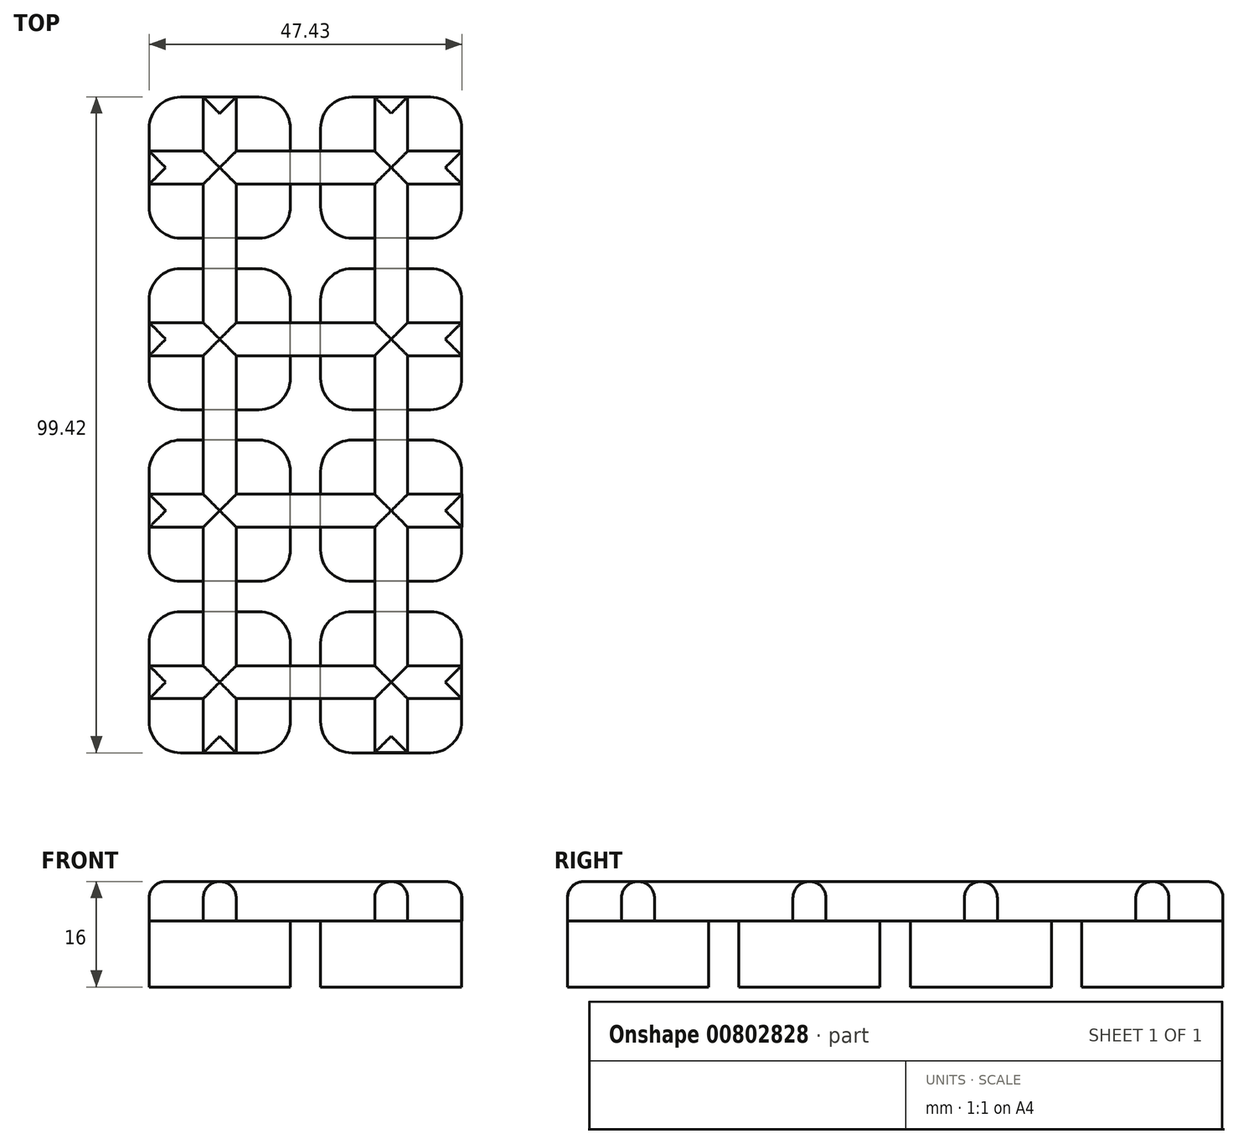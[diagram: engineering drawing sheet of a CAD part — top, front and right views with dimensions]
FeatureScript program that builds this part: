
annotation { "Feature Type Name" : "Feature", "Feature Type Description" : "" }
export const myFeature = defineFeature(function(context is Context, id is Id, definition is map)
    precondition{}
    {
        {
            var Q0;
            Q0=qCreatedBy(makeId("Top.planeOp"),FACE);
            var sketch = newSketch(context, id + "F0", { "sketchPlane" : qUnion([Q0])});
            skLineSegment(sketch, "E0.bottom", {"start": v(10.7, -10.7) * mm, "end": v(-10.7, -10.7) * mm});
            skLineSegment(sketch, "E0.top", {"start": v(10.7, 10.7) * mm, "end": v(-10.7, 10.7) * mm});
            skLineSegment(sketch, "E0.left", {"start": v(10.7, -10.7) * mm, "end": v(10.7, 10.7) * mm});
            skLineSegment(sketch, "E0.right", {"start": v(-10.7, -10.7) * mm, "end": v(-10.7, 10.7) * mm});
            skPoint(sketch, "E0.middle", {"position": v(0, 0) * mm});
            skLineSegment(sketch, "E1.bottom", {"start": v(36.7, -10.7) * mm, "end": v(15.3, -10.7) * mm});
            skLineSegment(sketch, "E1.top", {"start": v(36.7, 10.7) * mm, "end": v(15.3, 10.7) * mm});
            skLineSegment(sketch, "E1.left", {"start": v(36.7, -10.7) * mm, "end": v(36.7, 10.7) * mm});
            skLineSegment(sketch, "E1.right", {"start": v(15.3, -10.7) * mm, "end": v(15.3, 10.7) * mm});
            skPoint(sketch, "E1.middle", {"position": v(26, 0) * mm});
            skLineSegment(sketch, "E2.bottom", {"start": v(10.7, -36.7) * mm, "end": v(-10.7, -36.7) * mm});
            skLineSegment(sketch, "E2.top", {"start": v(10.7, -15.3) * mm, "end": v(-10.7, -15.3) * mm});
            skLineSegment(sketch, "E2.left", {"start": v(10.7, -36.7) * mm, "end": v(10.7, -15.3) * mm});
            skLineSegment(sketch, "E2.right", {"start": v(-10.7, -36.7) * mm, "end": v(-10.7, -15.3) * mm});
            skPoint(sketch, "E2.middle", {"position": v(0, -26) * mm});
            skLineSegment(sketch, "E3.bottom", {"start": v(36.7, -36.7) * mm, "end": v(15.3, -36.7) * mm});
            skLineSegment(sketch, "E3.top", {"start": v(36.7, -15.3) * mm, "end": v(15.3, -15.3) * mm});
            skLineSegment(sketch, "E3.left", {"start": v(36.7, -36.7) * mm, "end": v(36.7, -15.3) * mm});
            skLineSegment(sketch, "E3.right", {"start": v(15.3, -36.7) * mm, "end": v(15.3, -15.3) * mm});
            skPoint(sketch, "E3.middle", {"position": v(26, -26) * mm});
            skLineSegment(sketch, "E4.bottom", {"start": v(10.7, -62.7) * mm, "end": v(-10.7, -62.7) * mm});
            skLineSegment(sketch, "E4.top", {"start": v(10.7, -41.3) * mm, "end": v(-10.7, -41.3) * mm});
            skLineSegment(sketch, "E4.left", {"start": v(10.7, -62.7) * mm, "end": v(10.7, -41.3) * mm});
            skLineSegment(sketch, "E4.right", {"start": v(-10.7, -62.7) * mm, "end": v(-10.7, -41.3) * mm});
            skPoint(sketch, "E4.middle", {"position": v(0, -52) * mm});
            skLineSegment(sketch, "E5.bottom", {"start": v(36.7, -62.7) * mm, "end": v(15.3, -62.7) * mm});
            skLineSegment(sketch, "E5.top", {"start": v(36.7, -41.3) * mm, "end": v(15.3, -41.3) * mm});
            skLineSegment(sketch, "E5.left", {"start": v(36.7, -62.7) * mm, "end": v(36.7, -41.3) * mm});
            skLineSegment(sketch, "E5.right", {"start": v(15.3, -62.7) * mm, "end": v(15.3, -41.3) * mm});
            skPoint(sketch, "E5.middle", {"position": v(26, -52) * mm});
            skLineSegment(sketch, "E6.bottom", {"start": v(10.7, -88.7) * mm, "end": v(-10.7, -88.7) * mm});
            skLineSegment(sketch, "E6.top", {"start": v(10.7, -67.3) * mm, "end": v(-10.7, -67.3) * mm});
            skLineSegment(sketch, "E6.left", {"start": v(10.7, -88.7) * mm, "end": v(10.7, -67.3) * mm});
            skLineSegment(sketch, "E6.right", {"start": v(-10.7, -88.7) * mm, "end": v(-10.7, -67.3) * mm});
            skPoint(sketch, "E6.middle", {"position": v(0, -78) * mm});
            skLineSegment(sketch, "E7.bottom", {"start": v(36.7, -88.7) * mm, "end": v(15.3, -88.7) * mm});
            skLineSegment(sketch, "E7.top", {"start": v(36.7, -67.3) * mm, "end": v(15.3, -67.3) * mm});
            skLineSegment(sketch, "E7.left", {"start": v(36.7, -88.7) * mm, "end": v(36.7, -67.3) * mm});
            skLineSegment(sketch, "E7.right", {"start": v(15.3, -88.7) * mm, "end": v(15.3, -67.3) * mm});
            skPoint(sketch, "E7.middle", {"position": v(26, -78) * mm});
            skSolve(sketch);
        }
        {
            var Q0;
            Q0 = qSketchRegion(id + "F0", true);
            extrude(context, id + "F1", {"entities" : qUnion([Q0]), "depth" : 10 * mm, "offsetDistance" : 25 * mm});
        }
        {
            var Q0;
            Q0=makeQuery(id+"F1.opExtrude","CAP_FACE",FACE,{"disambiguationData":[OSD([sQuery(id+"F0.wireOp",EDGE,"E0.bottom"),sQuery(id+"F0.wireOp",EDGE,"E0.top"),sQuery(id+"F0.wireOp",EDGE,"E0.left"),sQuery(id+"F0.wireOp",EDGE,"E0.right")])],"isStart":false});
            var sketch = newSketch(context, id + "F2", { "sketchPlane" : qUnion([Q0])});
            skLineSegment(sketch, "E8.bottom", {"start": v(-10.7, 2.5) * mm, "end": v(-2.5, 2.5) * mm});
            skLineSegment(sketch, "E8.top", {"start": v(-10.7, -2.5) * mm, "end": v(-2.5, -2.5) * mm});
            skLineSegment(sketch, "E8.left", {"start": v(-10.7, 2.5) * mm, "end": v(-10.7, -2.5) * mm});
            skLineSegment(sketch, "E8.right", {"start": v(36.7, 2.5) * mm, "end": v(36.7, -2.5) * mm});
            skLineSegment(sketch, "E9.bottom", {"start": v(-2.5, 10.7) * mm, "end": v(2.5, 10.7) * mm});
            skLineSegment(sketch, "E9.top", {"start": v(-2.5, -88.7) * mm, "end": v(2.5, -88.7) * mm});
            skLineSegment(sketch, "E9.left", {"start": v(-2.5, 10.7) * mm, "end": v(-2.5, 2.5) * mm});
            skLineSegment(sketch, "E9.right", {"start": v(2.5, 10.7) * mm, "end": v(2.5, 2.5) * mm});
            skLineSegment(sketch, "E10.bottom", {"start": v(23.5, 10.72) * mm, "end": v(28.5, 10.72) * mm});
            skLineSegment(sketch, "E10.top", {"start": v(23.5, -88.68) * mm, "end": v(28.5, -88.68) * mm});
            skLineSegment(sketch, "E10.left", {"start": v(23.5, 10.72) * mm, "end": v(23.5, 2.5) * mm});
            skLineSegment(sketch, "E10.right", {"start": v(28.5, 10.72) * mm, "end": v(28.5, 2.5) * mm});
            skLineSegment(sketch, "E11.bottom", {"start": v(-10.7, -23.5) * mm, "end": v(-2.5, -23.5) * mm});
            skLineSegment(sketch, "E11.top", {"start": v(-10.7, -28.5) * mm, "end": v(-2.5, -28.5) * mm});
            skLineSegment(sketch, "E11.left", {"start": v(-10.7, -23.5) * mm, "end": v(-10.7, -28.5) * mm});
            skLineSegment(sketch, "E11.right", {"start": v(36.7, -23.5) * mm, "end": v(36.7, -28.5) * mm});
            skLineSegment(sketch, "E12.bottom", {"start": v(-10.67, -49.5) * mm, "end": v(-2.5, -49.5) * mm});
            skLineSegment(sketch, "E12.top", {"start": v(-10.67, -54.5) * mm, "end": v(-2.5, -54.5) * mm});
            skLineSegment(sketch, "E12.left", {"start": v(-10.67, -49.5) * mm, "end": v(-10.67, -54.5) * mm});
            skLineSegment(sketch, "E12.right", {"start": v(36.73, -49.5) * mm, "end": v(36.73, -54.5) * mm});
            skLineSegment(sketch, "E13.bottom", {"start": v(-10.7, -75.5) * mm, "end": v(-2.5, -75.5) * mm});
            skLineSegment(sketch, "E13.top", {"start": v(-10.7, -80.5) * mm, "end": v(-2.5, -80.5) * mm});
            skLineSegment(sketch, "E13.left", {"start": v(-10.7, -75.5) * mm, "end": v(-10.7, -80.5) * mm});
            skLineSegment(sketch, "E13.right", {"start": v(36.7, -75.5) * mm, "end": v(36.7, -80.5) * mm});
            skLineSegment(sketch, "E14.trimOffspring", {"start": v(-2.5, -28.5) * mm, "end": v(-2.5, -49.5) * mm});
            skLineSegment(sketch, "E15.trimOffspring", {"start": v(2.5, -23.5) * mm, "end": v(23.5, -23.5) * mm});
            skLineSegment(sketch, "E16.trimOffspring", {"start": v(2.5, -28.5) * mm, "end": v(2.5, -49.5) * mm});
            skLineSegment(sketch, "E17.trimOffspring", {"start": v(2.5, -28.5) * mm, "end": v(23.5, -28.5) * mm});
            skLineSegment(sketch, "E18.trimOffspring", {"start": v(28.5, -23.5) * mm, "end": v(36.7, -23.5) * mm});
            skLineSegment(sketch, "E19.trimOffspring", {"start": v(23.5, -28.5) * mm, "end": v(23.5, -49.5) * mm});
            skLineSegment(sketch, "E20.trimOffspring", {"start": v(28.5, -28.5) * mm, "end": v(36.7, -28.5) * mm});
            skLineSegment(sketch, "E21.trimOffspring", {"start": v(28.5, -28.5) * mm, "end": v(28.5, -49.5) * mm});
            skLineSegment(sketch, "E22.trimOffspring", {"start": v(28.5, -49.5) * mm, "end": v(36.73, -49.5) * mm});
            skLineSegment(sketch, "E23.trimOffspring", {"start": v(23.5, -54.5) * mm, "end": v(23.5, -75.5) * mm});
            skLineSegment(sketch, "E24.trimOffspring", {"start": v(28.5, -54.5) * mm, "end": v(28.5, -75.5) * mm});
            skLineSegment(sketch, "E25.trimOffspring", {"start": v(28.5, -54.5) * mm, "end": v(36.73, -54.5) * mm});
            skLineSegment(sketch, "E26.trimOffspring", {"start": v(-2.5, -54.5) * mm, "end": v(-2.5, -75.5) * mm});
            skLineSegment(sketch, "E27.trimOffspring", {"start": v(2.5, -49.5) * mm, "end": v(23.5, -49.5) * mm});
            skLineSegment(sketch, "E28.trimOffspring", {"start": v(2.5, -54.5) * mm, "end": v(2.5, -75.5) * mm});
            skLineSegment(sketch, "E29.trimOffspring", {"start": v(2.5, -54.5) * mm, "end": v(23.5, -54.5) * mm});
            skLineSegment(sketch, "E30.trimOffspring", {"start": v(2.5, -75.5) * mm, "end": v(23.5, -75.5) * mm});
            skLineSegment(sketch, "E31.trimOffspring", {"start": v(-2.5, -80.5) * mm, "end": v(-2.5, -88.7) * mm});
            skLineSegment(sketch, "E32.trimOffspring", {"start": v(2.5, -80.5) * mm, "end": v(23.5, -80.5) * mm});
            skLineSegment(sketch, "E33.trimOffspring", {"start": v(2.5, -80.5) * mm, "end": v(2.5, -88.7) * mm});
            skLineSegment(sketch, "E34.trimOffspring", {"start": v(23.5, -80.5) * mm, "end": v(23.5, -88.68) * mm});
            skLineSegment(sketch, "E35.trimOffspring", {"start": v(28.5, -75.5) * mm, "end": v(36.7, -75.5) * mm});
            skLineSegment(sketch, "E36.trimOffspring", {"start": v(28.5, -80.5) * mm, "end": v(28.5, -88.68) * mm});
            skLineSegment(sketch, "E37.trimOffspring", {"start": v(28.5, -80.5) * mm, "end": v(36.7, -80.5) * mm});
            skLineSegment(sketch, "E38.trimOffspring", {"start": v(2.5, 2.5) * mm, "end": v(23.5, 2.5) * mm});
            skLineSegment(sketch, "E39.trimOffspring", {"start": v(-2.5, -2.5) * mm, "end": v(-2.5, -23.5) * mm});
            skLineSegment(sketch, "E40.trimOffspring", {"start": v(2.5, -2.5) * mm, "end": v(23.5, -2.5) * mm});
            skLineSegment(sketch, "E41.trimOffspring", {"start": v(2.5, -2.5) * mm, "end": v(2.5, -23.5) * mm});
            skLineSegment(sketch, "E42.trimOffspring", {"start": v(23.5, -2.5) * mm, "end": v(23.5, -23.5) * mm});
            skLineSegment(sketch, "E43.trimOffspring", {"start": v(28.5, 2.5) * mm, "end": v(36.7, 2.5) * mm});
            skLineSegment(sketch, "E44.trimOffspring", {"start": v(28.5, -2.5) * mm, "end": v(28.5, -23.5) * mm});
            skLineSegment(sketch, "E45.trimOffspring", {"start": v(28.5, -2.5) * mm, "end": v(36.7, -2.5) * mm});
            skSolve(sketch);
        }
        {
            var Q0;
            Q0 = qSketchRegion(id + "F2", true);
            extrude(context, id + "F3", {"entities" : qUnion([Q0]), "depth" : 6 * mm, "offsetDistance" : 25 * mm});
        }
        {
            var Q0;
            Q0=makeQuery(id+"F1.opExtrude","SWEPT_EDGE",EDGE,{"disambiguationData":[OSD([sQuery(id+"F0.wireOp",EDGE,"E7.bottom"),sQuery(id+"F0.wireOp",EDGE,"E7.left")])]});
            var Q1;
            Q1=makeQuery(id+"F1.opExtrude","SWEPT_EDGE",EDGE,{"disambiguationData":[OSD([sQuery(id+"F0.wireOp",EDGE,"E7.bottom"),sQuery(id+"F0.wireOp",EDGE,"E7.right")])]});
            var Q2;
            Q2=makeQuery(id+"F1.opExtrude","SWEPT_EDGE",EDGE,{"disambiguationData":[OSD([sQuery(id+"F0.wireOp",EDGE,"E6.bottom"),sQuery(id+"F0.wireOp",EDGE,"E6.left")])]});
            var Q3;
            Q3=makeQuery(id+"F1.opExtrude","SWEPT_EDGE",EDGE,{"disambiguationData":[OSD([sQuery(id+"F0.wireOp",EDGE,"E6.bottom"),sQuery(id+"F0.wireOp",EDGE,"E6.right")])]});
            var Q4;
            Q4=makeQuery(id+"F1.opExtrude","SWEPT_EDGE",EDGE,{"disambiguationData":[OSD([sQuery(id+"F0.wireOp",EDGE,"E7.top"),sQuery(id+"F0.wireOp",EDGE,"E7.left")])]});
            var Q5;
            Q5=makeQuery(id+"F1.opExtrude","SWEPT_EDGE",EDGE,{"disambiguationData":[OSD([sQuery(id+"F0.wireOp",EDGE,"E5.bottom"),sQuery(id+"F0.wireOp",EDGE,"E5.left")])]});
            var Q6;
            Q6=makeQuery(id+"F1.opExtrude","SWEPT_EDGE",EDGE,{"disambiguationData":[OSD([sQuery(id+"F0.wireOp",EDGE,"E5.top"),sQuery(id+"F0.wireOp",EDGE,"E5.left")])]});
            var Q7;
            Q7=makeQuery(id+"F1.opExtrude","SWEPT_EDGE",EDGE,{"disambiguationData":[OSD([sQuery(id+"F0.wireOp",EDGE,"E3.bottom"),sQuery(id+"F0.wireOp",EDGE,"E3.left")])]});
            var Q8;
            Q8=makeQuery(id+"F1.opExtrude","SWEPT_EDGE",EDGE,{"disambiguationData":[OSD([sQuery(id+"F0.wireOp",EDGE,"E3.top"),sQuery(id+"F0.wireOp",EDGE,"E3.left")])]});
            var Q9;
            Q9=makeQuery(id+"F1.opExtrude","SWEPT_EDGE",EDGE,{"disambiguationData":[OSD([sQuery(id+"F0.wireOp",EDGE,"E1.bottom"),sQuery(id+"F0.wireOp",EDGE,"E1.left")])]});
            var Q10;
            Q10=makeQuery(id+"F1.opExtrude","SWEPT_EDGE",EDGE,{"disambiguationData":[OSD([sQuery(id+"F0.wireOp",EDGE,"E1.top"),sQuery(id+"F0.wireOp",EDGE,"E1.left")])]});
            var Q11;
            Q11=makeQuery(id+"F1.opExtrude","SWEPT_EDGE",EDGE,{"disambiguationData":[OSD([sQuery(id+"F0.wireOp",EDGE,"E4.bottom"),sQuery(id+"F0.wireOp",EDGE,"E4.left")])]});
            var Q12;
            Q12=makeQuery(id+"F1.opExtrude","SWEPT_EDGE",EDGE,{"disambiguationData":[OSD([sQuery(id+"F0.wireOp",EDGE,"E5.bottom"),sQuery(id+"F0.wireOp",EDGE,"E5.right")])]});
            var Q13;
            Q13=makeQuery(id+"F1.opExtrude","SWEPT_EDGE",EDGE,{"disambiguationData":[OSD([sQuery(id+"F0.wireOp",EDGE,"E2.bottom"),sQuery(id+"F0.wireOp",EDGE,"E2.left")])]});
            var Q14;
            Q14=makeQuery(id+"F1.opExtrude","SWEPT_EDGE",EDGE,{"disambiguationData":[OSD([sQuery(id+"F0.wireOp",EDGE,"E3.bottom"),sQuery(id+"F0.wireOp",EDGE,"E3.right")])]});
            var Q15;
            Q15=makeQuery(id+"F1.opExtrude","SWEPT_EDGE",EDGE,{"disambiguationData":[OSD([sQuery(id+"F0.wireOp",EDGE,"E0.bottom"),sQuery(id+"F0.wireOp",EDGE,"E0.left")])]});
            var Q16;
            Q16=makeQuery(id+"F1.opExtrude","SWEPT_EDGE",EDGE,{"disambiguationData":[OSD([sQuery(id+"F0.wireOp",EDGE,"E1.bottom"),sQuery(id+"F0.wireOp",EDGE,"E1.right")])]});
            var Q17;
            Q17=makeQuery(id+"F1.opExtrude","SWEPT_EDGE",EDGE,{"disambiguationData":[OSD([sQuery(id+"F0.wireOp",EDGE,"E2.top"),sQuery(id+"F0.wireOp",EDGE,"E2.left")])]});
            var Q18;
            Q18=makeQuery(id+"F1.opExtrude","SWEPT_EDGE",EDGE,{"disambiguationData":[OSD([sQuery(id+"F0.wireOp",EDGE,"E0.top"),sQuery(id+"F0.wireOp",EDGE,"E0.left")])]});
            var Q19;
            Q19=makeQuery(id+"F1.opExtrude","SWEPT_EDGE",EDGE,{"disambiguationData":[OSD([sQuery(id+"F0.wireOp",EDGE,"E1.top"),sQuery(id+"F0.wireOp",EDGE,"E1.right")])]});
            var Q20;
            Q20=makeQuery(id+"F1.opExtrude","SWEPT_EDGE",EDGE,{"disambiguationData":[OSD([sQuery(id+"F0.wireOp",EDGE,"E3.top"),sQuery(id+"F0.wireOp",EDGE,"E3.right")])]});
            var Q21;
            Q21=makeQuery(id+"F1.opExtrude","SWEPT_EDGE",EDGE,{"disambiguationData":[OSD([sQuery(id+"F0.wireOp",EDGE,"E5.top"),sQuery(id+"F0.wireOp",EDGE,"E5.right")])]});
            var Q22;
            Q22=makeQuery(id+"F1.opExtrude","SWEPT_EDGE",EDGE,{"disambiguationData":[OSD([sQuery(id+"F0.wireOp",EDGE,"E7.top"),sQuery(id+"F0.wireOp",EDGE,"E7.right")])]});
            var Q23;
            Q23=makeQuery(id+"F1.opExtrude","SWEPT_EDGE",EDGE,{"disambiguationData":[OSD([sQuery(id+"F0.wireOp",EDGE,"E4.top"),sQuery(id+"F0.wireOp",EDGE,"E4.right")])]});
            var Q24;
            Q24=makeQuery(id+"F1.opExtrude","SWEPT_EDGE",EDGE,{"disambiguationData":[OSD([sQuery(id+"F0.wireOp",EDGE,"E0.top"),sQuery(id+"F0.wireOp",EDGE,"E0.right")])]});
            var Q25;
            Q25=makeQuery(id+"F1.opExtrude","SWEPT_EDGE",EDGE,{"disambiguationData":[OSD([sQuery(id+"F0.wireOp",EDGE,"E0.bottom"),sQuery(id+"F0.wireOp",EDGE,"E0.right")])]});
            var Q26;
            Q26=makeQuery(id+"F1.opExtrude","SWEPT_EDGE",EDGE,{"disambiguationData":[OSD([sQuery(id+"F0.wireOp",EDGE,"E2.top"),sQuery(id+"F0.wireOp",EDGE,"E2.right")])]});
            var Q27;
            Q27=makeQuery(id+"F1.opExtrude","SWEPT_EDGE",EDGE,{"disambiguationData":[OSD([sQuery(id+"F0.wireOp",EDGE,"E2.bottom"),sQuery(id+"F0.wireOp",EDGE,"E2.right")])]});
            var Q28;
            Q28=makeQuery(id+"F1.opExtrude","SWEPT_EDGE",EDGE,{"disambiguationData":[OSD([sQuery(id+"F0.wireOp",EDGE,"E4.bottom"),sQuery(id+"F0.wireOp",EDGE,"E4.right")])]});
            var Q29;
            Q29=makeQuery(id+"F1.opExtrude","SWEPT_EDGE",EDGE,{"disambiguationData":[OSD([sQuery(id+"F0.wireOp",EDGE,"E4.top"),sQuery(id+"F0.wireOp",EDGE,"E4.left")])]});
            var Q30;
            Q30=makeQuery(id+"F1.opExtrude","SWEPT_EDGE",EDGE,{"disambiguationData":[OSD([sQuery(id+"F0.wireOp",EDGE,"E6.top"),sQuery(id+"F0.wireOp",EDGE,"E6.right")])]});
            var Q31;
            Q31=makeQuery(id+"F1.opExtrude","SWEPT_EDGE",EDGE,{"disambiguationData":[OSD([sQuery(id+"F0.wireOp",EDGE,"E6.top"),sQuery(id+"F0.wireOp",EDGE,"E6.left")])]});
            fillet(context, id + "F4", {"entities" : qUnion([Q0, Q1, Q2, Q3, Q4, Q5, Q6, Q7, Q8, Q9, Q10, Q11, Q12, Q13, Q14, Q15, Q16, Q17, Q18, Q19, Q20, Q21, Q22, Q23, Q24, Q25, Q26, Q27, Q28, Q29, Q30, Q31]), "radius" : 4.75 * mm, "tangentPropagation" : true, "allowEdgeOverflow" : false});
        }
        {
            var Q0;
            Q0=makeQuery(id+"F3.opExtrude","CAP_EDGE",EDGE,{"disambiguationData":[OSD([sQuery(id+"F2.wireOp",EDGE,"E38.trimOffspring")])],"isStart":false});
            var Q1;
            Q1=makeQuery(id+"F3.opExtrude","CAP_EDGE",EDGE,{"disambiguationData":[OSD([sQuery(id+"F2.wireOp",EDGE,"E10.bottom")])],"isStart":false});
            var Q2;
            Q2=makeQuery(id+"F3.opExtrude","CAP_EDGE",EDGE,{"disambiguationData":[OSD([sQuery(id+"F2.wireOp",EDGE,"E10.left")])],"isStart":false});
            var Q3;
            Q3=makeQuery(id+"F3.opExtrude","CAP_EDGE",EDGE,{"disambiguationData":[OSD([sQuery(id+"F2.wireOp",EDGE,"E9.bottom")])],"isStart":false});
            var Q4;
            Q4=makeQuery(id+"F3.opExtrude","CAP_EDGE",EDGE,{"disambiguationData":[OSD([sQuery(id+"F2.wireOp",EDGE,"E11.bottom")])],"isStart":false});
            var Q5;
            Q5=makeQuery(id+"F3.opExtrude","CAP_EDGE",EDGE,{"disambiguationData":[OSD([sQuery(id+"F2.wireOp",EDGE,"E9.left")])],"isStart":false});
            var Q6;
            Q6=makeQuery(id+"F3.opExtrude","CAP_EDGE",EDGE,{"disambiguationData":[OSD([sQuery(id+"F2.wireOp",EDGE,"E9.right")])],"isStart":false});
            var Q7;
            Q7=makeQuery(id+"F3.opExtrude","CAP_EDGE",EDGE,{"disambiguationData":[OSD([sQuery(id+"F2.wireOp",EDGE,"E8.bottom")])],"isStart":false});
            var Q8;
            Q8=makeQuery(id+"F3.opExtrude","CAP_EDGE",EDGE,{"disambiguationData":[OSD([sQuery(id+"F2.wireOp",EDGE,"E10.right")])],"isStart":false});
            var Q9;
            Q9=makeQuery(id+"F3.opExtrude","CAP_EDGE",EDGE,{"disambiguationData":[OSD([sQuery(id+"F2.wireOp",EDGE,"E43.trimOffspring")])],"isStart":false});
            var Q10;
            Q10=makeQuery(id+"F3.opExtrude","CAP_EDGE",EDGE,{"disambiguationData":[OSD([sQuery(id+"F2.wireOp",EDGE,"E8.right")])],"isStart":false});
            var Q11;
            Q11=makeQuery(id+"F3.opExtrude","CAP_EDGE",EDGE,{"disambiguationData":[OSD([sQuery(id+"F2.wireOp",EDGE,"E8.left")])],"isStart":false});
            var Q12;
            Q12=makeQuery(id+"F3.opExtrude","CAP_EDGE",EDGE,{"disambiguationData":[OSD([sQuery(id+"F2.wireOp",EDGE,"E8.top")])],"isStart":false});
            var Q13;
            Q13=makeQuery(id+"F3.opExtrude","CAP_EDGE",EDGE,{"disambiguationData":[OSD([sQuery(id+"F2.wireOp",EDGE,"E39.trimOffspring")])],"isStart":false});
            var Q14;
            Q14=makeQuery(id+"F3.opExtrude","CAP_EDGE",EDGE,{"disambiguationData":[OSD([sQuery(id+"F2.wireOp",EDGE,"E11.left")])],"isStart":false});
            var Q15;
            Q15=makeQuery(id+"F3.opExtrude","CAP_EDGE",EDGE,{"disambiguationData":[OSD([sQuery(id+"F2.wireOp",EDGE,"E11.top")])],"isStart":false});
            var Q16;
            Q16=makeQuery(id+"F3.opExtrude","CAP_EDGE",EDGE,{"disambiguationData":[OSD([sQuery(id+"F2.wireOp",EDGE,"E12.left")])],"isStart":false});
            var Q17;
            Q17=makeQuery(id+"F3.opExtrude","CAP_EDGE",EDGE,{"disambiguationData":[OSD([sQuery(id+"F2.wireOp",EDGE,"E12.bottom")])],"isStart":false});
            var Q18;
            Q18=makeQuery(id+"F3.opExtrude","CAP_EDGE",EDGE,{"disambiguationData":[OSD([sQuery(id+"F2.wireOp",EDGE,"E14.trimOffspring")])],"isStart":false});
            var Q19;
            Q19=makeQuery(id+"F3.opExtrude","CAP_EDGE",EDGE,{"disambiguationData":[OSD([sQuery(id+"F2.wireOp",EDGE,"E16.trimOffspring")])],"isStart":false});
            var Q20;
            Q20=makeQuery(id+"F3.opExtrude","CAP_EDGE",EDGE,{"disambiguationData":[OSD([sQuery(id+"F2.wireOp",EDGE,"E17.trimOffspring")])],"isStart":false});
            var Q21;
            Q21=makeQuery(id+"F3.opExtrude","CAP_FACE",FACE,{"disambiguationData":[OSD([sQuery(id+"F2.wireOp",EDGE,"E8.bottom"),sQuery(id+"F2.wireOp",EDGE,"E8.top"),sQuery(id+"F2.wireOp",EDGE,"E8.left"),sQuery(id+"F2.wireOp",EDGE,"E8.right"),sQuery(id+"F2.wireOp",EDGE,"E9.bottom"),sQuery(id+"F2.wireOp",EDGE,"E9.top"),sQuery(id+"F2.wireOp",EDGE,"E9.left"),sQuery(id+"F2.wireOp",EDGE,"E9.right"),sQuery(id+"F2.wireOp",EDGE,"E10.bottom"),sQuery(id+"F2.wireOp",EDGE,"E10.top"),sQuery(id+"F2.wireOp",EDGE,"E10.left"),sQuery(id+"F2.wireOp",EDGE,"E10.right"),sQuery(id+"F2.wireOp",EDGE,"E11.bottom"),sQuery(id+"F2.wireOp",EDGE,"E11.top"),sQuery(id+"F2.wireOp",EDGE,"E11.left"),sQuery(id+"F2.wireOp",EDGE,"E11.right"),sQuery(id+"F2.wireOp",EDGE,"E12.bottom"),sQuery(id+"F2.wireOp",EDGE,"E12.top"),sQuery(id+"F2.wireOp",EDGE,"E12.left"),sQuery(id+"F2.wireOp",EDGE,"E12.right"),sQuery(id+"F2.wireOp",EDGE,"E13.bottom"),sQuery(id+"F2.wireOp",EDGE,"E13.top"),sQuery(id+"F2.wireOp",EDGE,"E13.left"),sQuery(id+"F2.wireOp",EDGE,"E13.right"),sQuery(id+"F2.wireOp",EDGE,"E14.trimOffspring"),sQuery(id+"F2.wireOp",EDGE,"E15.trimOffspring"),sQuery(id+"F2.wireOp",EDGE,"E16.trimOffspring"),sQuery(id+"F2.wireOp",EDGE,"E17.trimOffspring"),sQuery(id+"F2.wireOp",EDGE,"E18.trimOffspring"),sQuery(id+"F2.wireOp",EDGE,"E19.trimOffspring"),sQuery(id+"F2.wireOp",EDGE,"E20.trimOffspring"),sQuery(id+"F2.wireOp",EDGE,"E21.trimOffspring"),sQuery(id+"F2.wireOp",EDGE,"E22.trimOffspring"),sQuery(id+"F2.wireOp",EDGE,"E23.trimOffspring"),sQuery(id+"F2.wireOp",EDGE,"E24.trimOffspring"),sQuery(id+"F2.wireOp",EDGE,"E25.trimOffspring"),sQuery(id+"F2.wireOp",EDGE,"E26.trimOffspring"),sQuery(id+"F2.wireOp",EDGE,"E27.trimOffspring"),sQuery(id+"F2.wireOp",EDGE,"E28.trimOffspring"),sQuery(id+"F2.wireOp",EDGE,"E29.trimOffspring"),sQuery(id+"F2.wireOp",EDGE,"E30.trimOffspring"),sQuery(id+"F2.wireOp",EDGE,"E31.trimOffspring"),sQuery(id+"F2.wireOp",EDGE,"E32.trimOffspring"),sQuery(id+"F2.wireOp",EDGE,"E33.trimOffspring"),sQuery(id+"F2.wireOp",EDGE,"E34.trimOffspring"),sQuery(id+"F2.wireOp",EDGE,"E35.trimOffspring"),sQuery(id+"F2.wireOp",EDGE,"E36.trimOffspring"),sQuery(id+"F2.wireOp",EDGE,"E37.trimOffspring"),sQuery(id+"F2.wireOp",EDGE,"E38.trimOffspring"),sQuery(id+"F2.wireOp",EDGE,"E39.trimOffspring"),sQuery(id+"F2.wireOp",EDGE,"E40.trimOffspring"),sQuery(id+"F2.wireOp",EDGE,"E41.trimOffspring"),sQuery(id+"F2.wireOp",EDGE,"E42.trimOffspring"),sQuery(id+"F2.wireOp",EDGE,"E43.trimOffspring"),sQuery(id+"F2.wireOp",EDGE,"E44.trimOffspring"),sQuery(id+"F2.wireOp",EDGE,"E45.trimOffspring")])],"isStart":false});
            fillet(context, id + "F5", {"entities" : qUnion([Q0, Q1, Q2, Q3, Q4, Q5, Q6, Q7, Q8, Q9, Q10, Q11, Q12, Q13, Q14, Q15, Q16, Q17, Q18, Q19, Q20, Q21]), "radius" : 2.5 * mm, "tangentPropagation" : true, "allowEdgeOverflow" : false});
        }
    });
